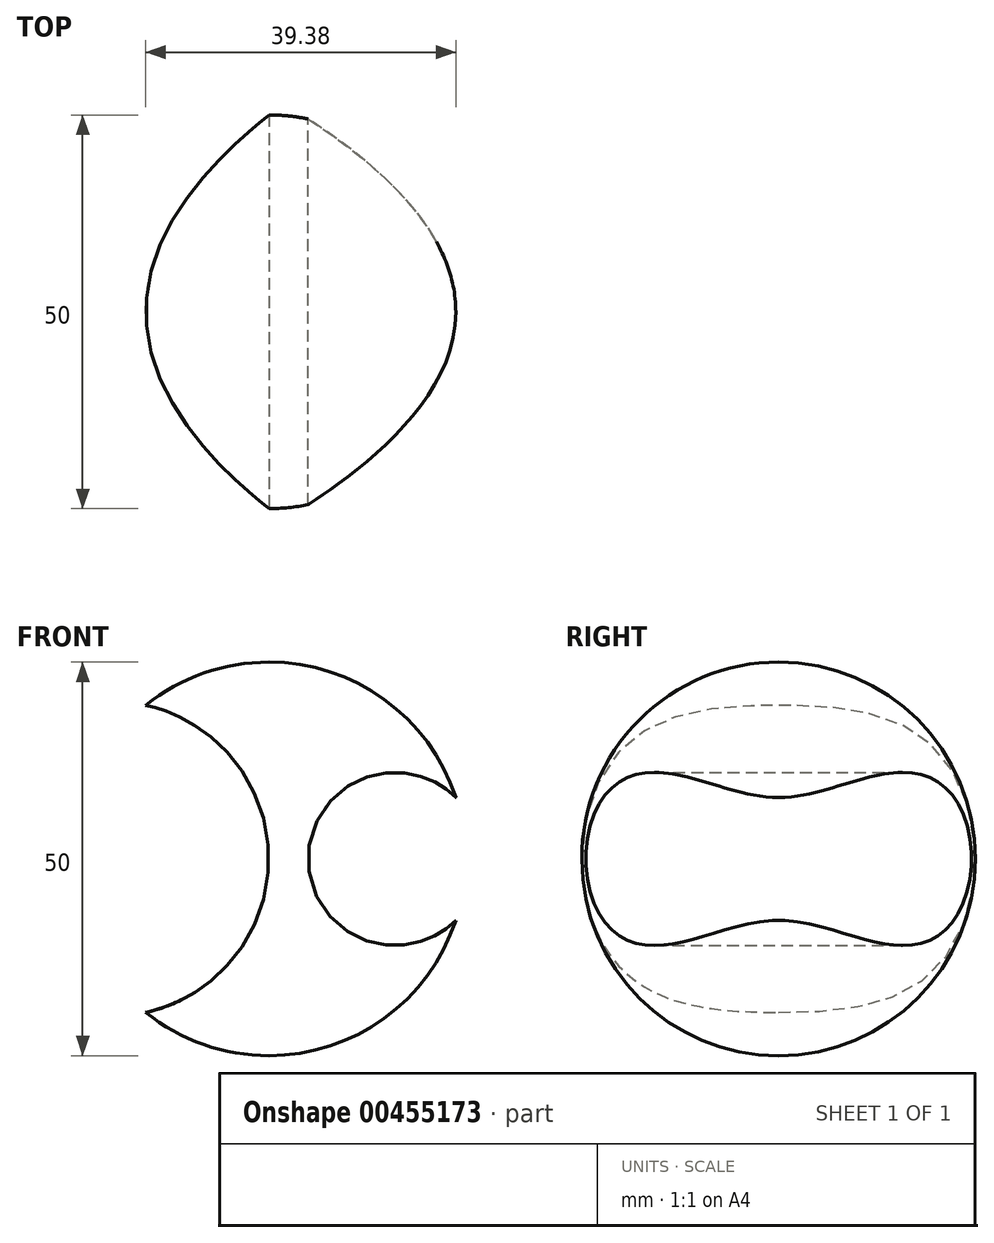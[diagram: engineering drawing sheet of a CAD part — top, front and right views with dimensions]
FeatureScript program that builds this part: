
annotation { "Feature Type Name" : "Feature", "Feature Type Description" : "" }
export const myFeature = defineFeature(function(context is Context, id is Id, definition is map)
    precondition{}
    {
        {
            var Q0;
            Q0=qCreatedBy(makeId("Front.planeOp"),FACE);
            var sketch = newSketch(context, id + "F0", { "sketchPlane" : qUnion([Q0])});
            skArc(sketch, "E0", {"start": v(0, -25) * mm, "mid": v(25, 0) * mm, "end": v(0, 25) * mm});
            skLineSegment(sketch, "E1", {"start": v(0, 25) * mm, "end": v(0, -25) * mm});
            skSolve(sketch);
        }
        {
            var Q0;
            Q0=makeQuery(id+"F0.imprint","IMPRINT",FACE,{"disambiguationData":[TD([[makeQuery(id+"F0.imprint","IMPRINT",EDGE,{"derivedFrom":sQuery(id+"F0.wireOp",EDGE,"E0")}),1.0]])]});
            var Q1;
            Q1=sQuery(id+"F0.wireOp",EDGE,"E1");
            revolve(context, id + "F1", {"entities" : qUnion([Q0]), "axis" : qUnion([Q1]), "revolveType" : RevolveType.FULL});
        }
        {
            var Q0;
            Q0=qCreatedBy(makeId("Front.planeOp"),FACE);
            var sketch = newSketch(context, id + "F2", { "sketchPlane" : qUnion([Q0])});
            skCircle(sketch, "E2", {"center": v(16, 0) * mm, "radius": 11 * mm});
            skSolve(sketch);
        }
        {
            var Q0;
            Q0=makeQuery(id+"F2.imprint","IMPRINT",FACE,{"disambiguationData":[TD([[makeQuery(id+"F2.imprint","IMPRINT",EDGE,{"derivedFrom":sQuery(id+"F2.wireOp",EDGE,"E2")}),1.0]])]});
            extrude(context, id + "F3", {"entities" : qUnion([Q0]), "operationType" : NewBodyOperationType.REMOVE, "endBound" : BoundingType.SYMMETRIC, "depth" : 50 * mm});
        }
        {
            var Q0;
            Q0=qCreatedBy(makeId("Front.planeOp"),FACE);
            var sketch = newSketch(context, id + "F4", { "sketchPlane" : qUnion([Q0])});
            skCircle(sketch, "E3", {"center": v(-20, 0) * mm, "radius": 20 * mm});
            skSolve(sketch);
        }
        {
            var Q0;
            Q0=makeQuery(id+"F4.imprint","IMPRINT",FACE,{"disambiguationData":[TD([[makeQuery(id+"F4.imprint","IMPRINT",EDGE,{"derivedFrom":sQuery(id+"F4.wireOp",EDGE,"E3")}),1.0]])]});
            extrude(context, id + "F5", {"entities" : qUnion([Q0]), "operationType" : NewBodyOperationType.REMOVE, "endBound" : BoundingType.SYMMETRIC, "oppositeDirection" : true, "depth" : 50 * mm});
        }
    });
